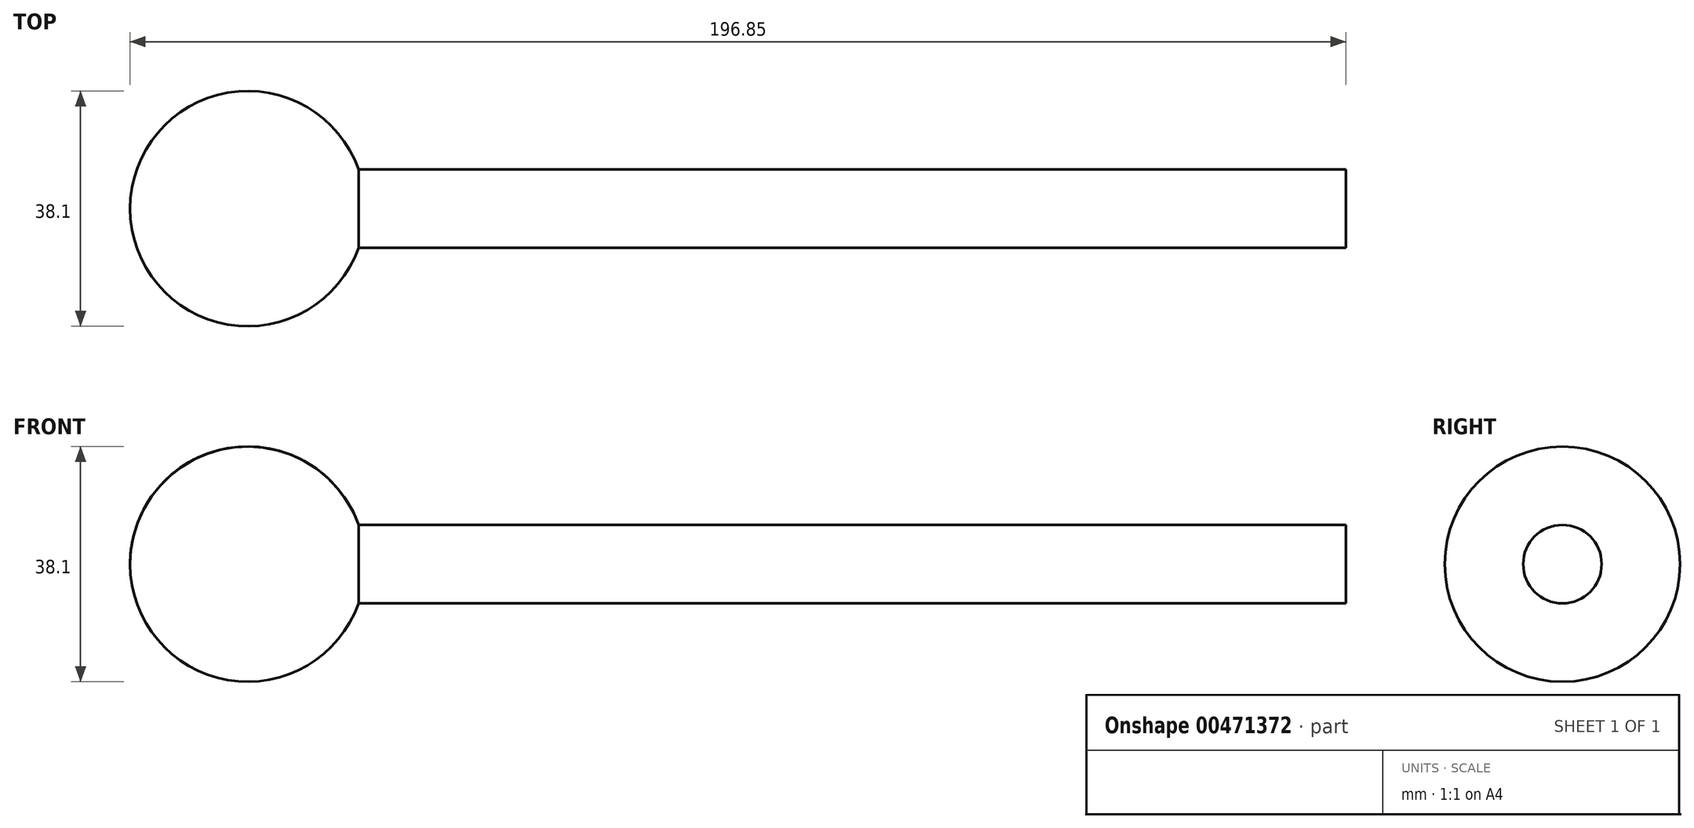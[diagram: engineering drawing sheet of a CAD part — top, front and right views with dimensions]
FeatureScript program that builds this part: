
annotation { "Feature Type Name" : "Feature", "Feature Type Description" : "" }
export const myFeature = defineFeature(function(context is Context, id is Id, definition is map)
    precondition{}
    {
        {
            var Q0;
            Q0=qCreatedBy(makeId("Front.planeOp"),FACE);
            var sketch = newSketch(context, id + "F0", { "sketchPlane" : qUnion([Q0])});
            skArc(sketch, "E0", {"start": v(19.05, 0) * mm, "mid": v(0, 19.05) * mm, "end": v(-19.05, 0) * mm});
            skLineSegment(sketch, "E1", {"start": v(177.8, 6.35) * mm, "end": v(17.96, 6.35) * mm});
            skLineSegment(sketch, "E2", {"start": v(19.05, 0) * mm, "end": v(177.8, 0) * mm});
            skLineSegment(sketch, "E3", {"start": v(177.8, 6.35) * mm, "end": v(177.8, 0) * mm});
            skLineSegment(sketch, "E4", {"start": v(19.05, 0) * mm, "end": v(-19.05, 0) * mm});
            skSolve(sketch);
        }
        {
            var Q0;
            {var subQ0=sQuery(id+"F0.wireOp",EDGE,"E1");Q0=makeQuery(id+"F0.imprint","IMPRINT",FACE,{"disambiguationData":[TD([[makeQuery(id+"F0.imprint","IMPRINT",EDGE,{"derivedFrom":subQ0}),1.0]])]});}
            var Q1;
            Q1=sQuery(id+"F0.wireOp",EDGE,"E2");
            revolve(context, id + "F1", {"entities" : qUnion([Q0]), "axis" : qUnion([Q1]), "revolveType" : RevolveType.FULL});
        }
        {
            var Q0;
            {var subQ0=sQuery(id+"F0.wireOp",EDGE,"E4");Q0=makeQuery(id+"F0.imprint","IMPRINT",FACE,{"disambiguationData":[TD([[makeQuery(id+"F0.imprint","IMPRINT",EDGE,{"derivedFrom":subQ0}),-1.0]])]});}
            var Q1;
            Q1=sQuery(id+"F0.wireOp",EDGE,"E2");
            revolve(context, id + "F2", {"operationType" : NewBodyOperationType.ADD, "entities" : qUnion([Q0]), "axis" : qUnion([Q1]), "revolveType" : RevolveType.FULL});
        }
    });
